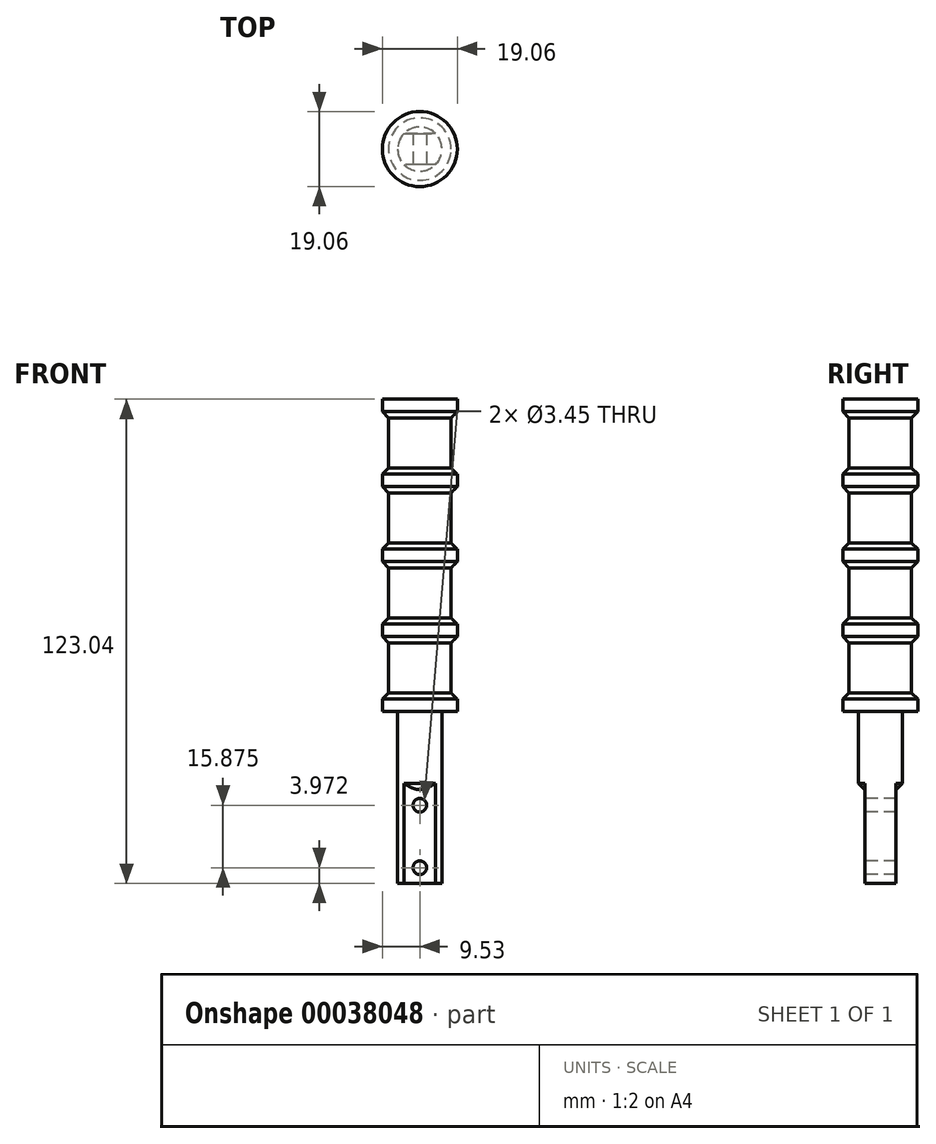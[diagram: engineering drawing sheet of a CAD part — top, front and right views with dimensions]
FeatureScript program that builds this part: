
annotation { "Feature Type Name" : "Feature", "Feature Type Description" : "" }
export const myFeature = defineFeature(function(context is Context, id is Id, definition is map)
    precondition{}
    {
        {
            var Q0;
            Q0=qCreatedBy(makeId("Top.planeOp"),FACE);
            var sketch = newSketch(context, id + "F0", { "sketchPlane" : qUnion([Q0])});
            skCircle(sketch, "E0", {"center": v(0, 0) * mm, "radius": 9.53 * mm});
            skSolve(sketch);
        }
        {
            var Q0;
            Q0 = qSketchRegion(id + "F0", true);
            extrude(context, id + "F1", {"entities" : qUnion([Q0]), "depth" : 152.4 * mm});
        }
        {
            var Q0;
            Q0=makeQuery(id+"F1.opExtrude","CAP_FACE",FACE,{"disambiguationData":[OSD([sQuery(id+"F0.wireOp",EDGE,"E0")])],"isStart":true});
            var sketch = newSketch(context, id + "F2", { "sketchPlane" : qUnion([Q0])});
            skCircle(sketch, "E1", {"center": v(0, 0) * mm, "radius": 5.61 * mm});
            skSolve(sketch);
        }
        {
            var Q0;
            Q0 = qSketchRegion(id + "F2", true);
            extrude(context, id + "F3", {"entities" : qUnion([Q0]), "operationType" : NewBodyOperationType.ADD, "depth" : 19.84 * mm});
        }
        {
            var Q0;
            Q0=makeQuery(id+"F3.opExtrude","CAP_FACE",FACE,{"disambiguationData":[OSD([sQuery(id+"F2.wireOp",EDGE,"E1")])],"isStart":false});
            var sketch = newSketch(context, id + "F4", { "sketchPlane" : qUnion([Q0])});
            skLineSegment(sketch, "E2.rect.bottom", {"start": v(3.97, 3.97) * mm, "end": v(-3.97, 3.97) * mm});
            skLineSegment(sketch, "E2.rect.top", {"start": v(3.97, -3.97) * mm, "end": v(-3.97, -3.97) * mm});
            skLineSegment(sketch, "E2.rect.left", {"start": v(3.97, 3.97) * mm, "end": v(3.97, -3.97) * mm, "construction": true});
            skLineSegment(sketch, "E2.rect.right", {"start": v(-3.97, 3.97) * mm, "end": v(-3.97, -3.97) * mm, "construction": true});
            skPoint(sketch, "E2.rect.middle", {"position": v(0, 0) * mm});
            skArc(sketch, "E3", {"start": v(3.97, -3.97) * mm, "mid": v(5.61, 0) * mm, "end": v(3.97, 3.97) * mm});
            skArc(sketch, "E4", {"start": v(-3.97, 3.97) * mm, "mid": v(-5.61, 0) * mm, "end": v(-3.97, -3.97) * mm});
            skSolve(sketch);
        }
        {
            var Q0;
            Q0 = qSketchRegion(id + "F4", true);
            extrude(context, id + "F5", {"entities" : qUnion([Q0]), "operationType" : NewBodyOperationType.ADD, "depth" : 23.8 * mm});
        }
        {
            var Q0;
            Q0=qCreatedBy(makeId("Front.planeOp"),FACE);
            var sketch = newSketch(context, id + "F6", { "sketchPlane" : qUnion([Q0])});
            skLineSegment(sketch, "E5.bottom", {"start": v(-7.94, 3.17) * mm, "end": v(-9.52, 3.17) * mm});
            skLineSegment(sketch, "E5.top", {"start": v(-7.94, 19.05) * mm, "end": v(-9.53, 19.05) * mm});
            skLineSegment(sketch, "E5.left", {"start": v(-7.94, 3.17) * mm, "end": v(-7.94, 19.05) * mm});
            skLineSegment(sketch, "E5.right", {"start": v(-9.52, 3.17) * mm, "end": v(-9.53, 19.05) * mm});
            skLineSegment(sketch, "E6", {"start": v(-7.94, 3.17) * mm, "end": v(0, 3.17) * mm, "construction": true});
            skLineSegment(sketch, "E7", {"start": v(0, 3.18) * mm, "end": v(0, 0) * mm, "construction": true});
            skLineSegment(sketch, "E8", {"start": v(-7.94, 19.05) * mm, "end": v(-7.94, 22.23) * mm, "construction": true});
            skLineSegment(sketch, "E9.bottom", {"start": v(-7.94, 22.23) * mm, "end": v(-9.53, 22.23) * mm});
            skLineSegment(sketch, "E9.top", {"start": v(-7.94, 38.1) * mm, "end": v(-9.53, 38.1) * mm});
            skLineSegment(sketch, "E9.left", {"start": v(-7.94, 22.23) * mm, "end": v(-7.94, 38.1) * mm});
            skLineSegment(sketch, "E9.right", {"start": v(-9.53, 22.23) * mm, "end": v(-9.53, 38.1) * mm});
            skLineSegment(sketch, "E10", {"start": v(-7.94, 38.1) * mm, "end": v(-7.94, 41.28) * mm, "construction": true});
            skLineSegment(sketch, "E11.bottom", {"start": v(-7.94, 41.28) * mm, "end": v(-9.53, 41.28) * mm});
            skLineSegment(sketch, "E11.top", {"start": v(-7.94, 57.15) * mm, "end": v(-9.53, 57.15) * mm});
            skLineSegment(sketch, "E11.left", {"start": v(-7.94, 41.28) * mm, "end": v(-7.94, 57.15) * mm});
            skLineSegment(sketch, "E11.right", {"start": v(-9.53, 41.28) * mm, "end": v(-9.53, 57.15) * mm});
            skLineSegment(sketch, "E12", {"start": v(-7.94, 57.15) * mm, "end": v(-7.94, 60.33) * mm, "construction": true});
            skLineSegment(sketch, "E13.bottom", {"start": v(-7.94, 60.33) * mm, "end": v(-9.53, 60.33) * mm});
            skLineSegment(sketch, "E13.top", {"start": v(-7.94, 76.2) * mm, "end": v(-9.53, 76.2) * mm});
            skLineSegment(sketch, "E13.left", {"start": v(-7.94, 60.33) * mm, "end": v(-7.94, 76.2) * mm});
            skLineSegment(sketch, "E13.right", {"start": v(-9.53, 60.33) * mm, "end": v(-9.53, 76.2) * mm});
            skLineSegment(sketch, "E14", {"start": v(-7.94, 76.2) * mm, "end": v(-7.94, 79.38) * mm, "construction": true});
            skLineSegment(sketch, "E15.bottom", {"start": v(-9.53, 79.38) * mm, "end": v(0, 79.38) * mm});
            skLineSegment(sketch, "E15.top", {"start": v(-9.53, 152.4) * mm, "end": v(0, 152.4) * mm});
            skLineSegment(sketch, "E15.left", {"start": v(-9.53, 79.38) * mm, "end": v(-9.53, 152.4) * mm});
            skLineSegment(sketch, "E15.right", {"start": v(0, 79.38) * mm, "end": v(0, 152.4) * mm});
            skSolve(sketch);
        }
        {
            var Q0;
            Q0 = qSketchRegion(id + "F6", true);
            var Q1;
            Q1=makeQuery(id+"F1.opExtrude","CAP_EDGE",EDGE,{"disambiguationData":[OSD([sQuery(id+"F0.wireOp",EDGE,"E0")])],"isStart":false});
            revolve(context, id + "F7", {"operationType" : NewBodyOperationType.REMOVE, "entities" : qUnion([Q0]), "axis" : qUnion([Q1]), "revolveType" : RevolveType.FULL, "oppositeDirection" : true});
        }
        {
            var Q0;
            Q0=makeQuery(id+"F5.opExtrude","SWEPT_FACE",FACE,{"disambiguationData":[OSD([sQuery(id+"F4.wireOp",EDGE,"E2.rect.bottom")])]});
            var sketch = newSketch(context, id + "F8", { "sketchPlane" : qUnion([Q0])});
            skLineSegment(sketch, "E16", {"start": v(0, -43.66) * mm, "end": v(0, -39.69) * mm, "construction": true});
            skLineSegment(sketch, "E17", {"start": v(0, -39.69) * mm, "end": v(0, -23.81) * mm, "construction": true});
            skCircle(sketch, "E18", {"center": v(0, -39.69) * mm, "radius": 1.73 * mm});
            skCircle(sketch, "E19", {"center": v(0, -23.81) * mm, "radius": 1.73 * mm});
            skSolve(sketch);
        }
        {
            var Q0;
            Q0 = qSketchRegion(id + "F8", true);
            var Q1;
            Q1=makeQuery(id+"F5.opExtrude","SWEPT_FACE",FACE,{"disambiguationData":[OSD([sQuery(id+"F4.wireOp",EDGE,"E2.rect.top")])]});
            extrude(context, id + "F9", {"entities" : qUnion([Q0]), "operationType" : NewBodyOperationType.REMOVE, "endBound" : BoundingType.UP_TO_SURFACE, "oppositeDirection" : true, "endBoundEntityFace" : qUnion([Q1]), "depth" : 25.4 * mm});
        }
        {
            var Q0;
            {var subQ0=sQuery(id+"F2.wireOp",EDGE,"E1");Q0=makeQuery(id+"F5.boolean.opBoolean","SPLIT",EDGE,{"disambiguationData":[TD([makeQuery(id+"F5.opExtrude","SWEPT_FACE",FACE,{"disambiguationData":[OSD([sQuery(id+"F4.wireOp",EDGE,"E2.rect.bottom")])]})])],"derivedFrom":makeQuery(id+"F3.opExtrude","CAP_EDGE",EDGE,{"disambiguationData":[OSD([subQ0])],"isStart":false})});}
            var Q1;
            {var subQ0=sQuery(id+"F2.wireOp",EDGE,"E1");Q1=makeQuery(id+"F5.boolean.opBoolean","SPLIT",EDGE,{"disambiguationData":[TD([makeQuery(id+"F5.opExtrude","SWEPT_FACE",FACE,{"disambiguationData":[OSD([sQuery(id+"F4.wireOp",EDGE,"E2.rect.top")])]})])],"derivedFrom":makeQuery(id+"F3.opExtrude","CAP_EDGE",EDGE,{"disambiguationData":[OSD([subQ0])],"isStart":false})});}
            chamfer(context, id + "F10", {"entities" : qUnion([Q0, Q1]), "width" : 1.64 * mm, "tangentPropagation" : true});
        }
        {
            var Q0;
            Q0=makeQuery(id+"F7.boolean.opBoolean","COPY",EDGE,{"derivedFrom":makeQuery(id+"F7.opRevolve","SWEPT_EDGE",EDGE,{"disambiguationData":[OSD([sQuery(id+"F6.wireOp",EDGE,"E5.bottom"),sQuery(id+"F6.wireOp",EDGE,"E5.left")])]})});
            var Q1;
            Q1=makeQuery(id+"F7.boolean.opBoolean","COPY",EDGE,{"derivedFrom":makeQuery(id+"F7.opRevolve","SWEPT_EDGE",EDGE,{"disambiguationData":[OSD([sQuery(id+"F6.wireOp",EDGE,"E5.top"),sQuery(id+"F6.wireOp",EDGE,"E5.left")])]})});
            var Q2;
            Q2=makeQuery(id+"F7.boolean.opBoolean","COPY",EDGE,{"derivedFrom":makeQuery(id+"F7.opRevolve","SWEPT_EDGE",EDGE,{"disambiguationData":[OSD([sQuery(id+"F6.wireOp",EDGE,"E9.top"),sQuery(id+"F6.wireOp",EDGE,"E9.left")])]})});
            var Q3;
            Q3=makeQuery(id+"F7.boolean.opBoolean","COPY",EDGE,{"derivedFrom":makeQuery(id+"F7.opRevolve","SWEPT_EDGE",EDGE,{"disambiguationData":[OSD([sQuery(id+"F6.wireOp",EDGE,"E11.top"),sQuery(id+"F6.wireOp",EDGE,"E11.left")])]})});
            var Q4;
            Q4=makeQuery(id+"F7.boolean.opBoolean","COPY",EDGE,{"derivedFrom":makeQuery(id+"F7.opRevolve","SWEPT_EDGE",EDGE,{"disambiguationData":[OSD([sQuery(id+"F6.wireOp",EDGE,"E13.top"),sQuery(id+"F6.wireOp",EDGE,"E13.left")])]})});
            var Q5;
            Q5=makeQuery(id+"F7.boolean.opBoolean","COPY",EDGE,{"derivedFrom":makeQuery(id+"F7.opRevolve","SWEPT_EDGE",EDGE,{"disambiguationData":[OSD([sQuery(id+"F6.wireOp",EDGE,"E13.bottom"),sQuery(id+"F6.wireOp",EDGE,"E13.left")])]})});
            var Q6;
            Q6=makeQuery(id+"F7.boolean.opBoolean","COPY",EDGE,{"derivedFrom":makeQuery(id+"F7.opRevolve","SWEPT_EDGE",EDGE,{"disambiguationData":[OSD([sQuery(id+"F6.wireOp",EDGE,"E11.bottom"),sQuery(id+"F6.wireOp",EDGE,"E11.left")])]})});
            var Q7;
            Q7=makeQuery(id+"F7.boolean.opBoolean","COPY",EDGE,{"derivedFrom":makeQuery(id+"F7.opRevolve","SWEPT_EDGE",EDGE,{"disambiguationData":[OSD([sQuery(id+"F6.wireOp",EDGE,"E9.bottom"),sQuery(id+"F6.wireOp",EDGE,"E9.left")])]})});
            chamfer(context, id + "F11", {"entities" : qUnion([Q0, Q1, Q2, Q3, Q4, Q5, Q6, Q7]), "width" : 1.59 * mm, "tangentPropagation" : true});
        }
    });
